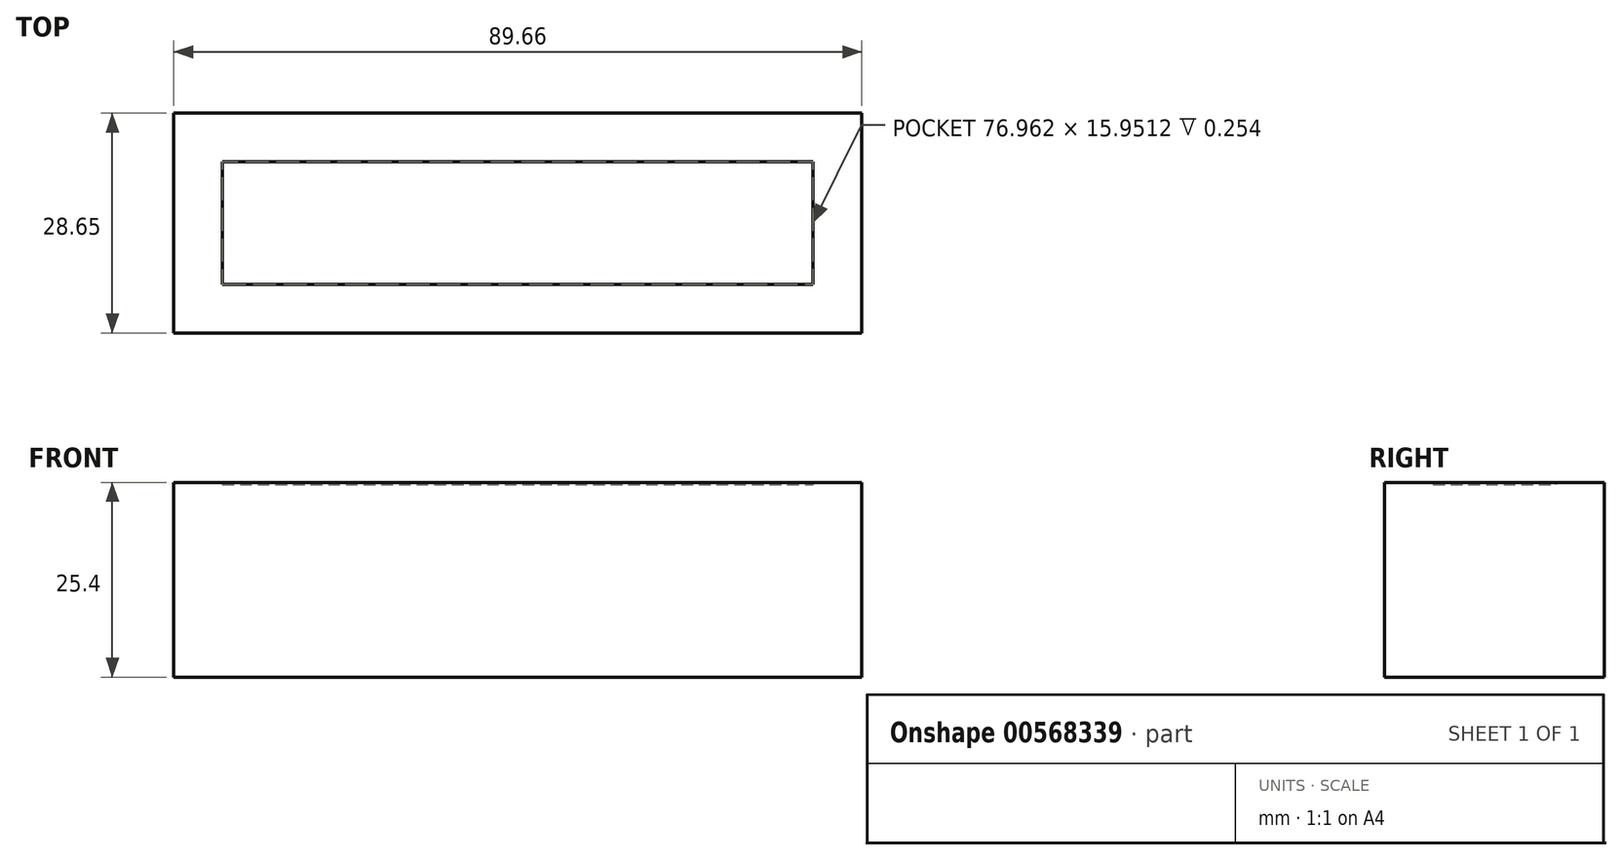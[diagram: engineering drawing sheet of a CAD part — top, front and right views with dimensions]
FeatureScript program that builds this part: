
annotation { "Feature Type Name" : "Feature", "Feature Type Description" : "" }
export const myFeature = defineFeature(function(context is Context, id is Id, definition is map)
    precondition{}
    {
        {
            var Q0;
            Q0=qCreatedBy(makeId("Top.planeOp"),FACE);
            var sketch = newSketch(context, id + "F0", { "sketchPlane" : qUnion([Q0])});
            skLineSegment(sketch, "E0.bottom", {"start": v(0, 0) * mm, "end": v(76.96, 0) * mm});
            skLineSegment(sketch, "E0.top", {"start": v(0, 15.95) * mm, "end": v(76.96, 15.95) * mm});
            skLineSegment(sketch, "E0.left", {"start": v(0, 0) * mm, "end": v(0, 15.95) * mm});
            skLineSegment(sketch, "E0.right", {"start": v(76.96, 0) * mm, "end": v(76.96, 15.95) * mm});
            skSolve(sketch);
        }
        {
            var Q0;
            Q0=makeQuery(id+"F0.imprint","IMPRINT",FACE,{"disambiguationData":[TD([[makeQuery(id+"F0.imprint","IMPRINT",EDGE,{"derivedFrom":sQuery(id+"F0.wireOp",EDGE,"E0.bottom")}),1.0]])]});
            extrude(context, id + "F1", {"entities" : qUnion([Q0]), "depth" : 0.25 * mm, "offsetDistance" : 25.4 * mm});
        }
        {
            var Q0;
            Q0=makeQuery(id+"F1.opExtrude","CAP_FACE",FACE,{"disambiguationData":[OSD([sQuery(id+"F0.wireOp",EDGE,"E0.bottom"),sQuery(id+"F0.wireOp",EDGE,"E0.top"),sQuery(id+"F0.wireOp",EDGE,"E0.left"),sQuery(id+"F0.wireOp",EDGE,"E0.right")])],"isStart":false});
            cPlane(context, id + "F2", {"entities" : qUnion([Q0]), "cplaneType" : CPlaneType.OFFSET, "offset" : 0 * mm, "width" : 152.4 * mm, "height" : 152.4 * mm});
        }
        {
            var Q0;
            Q0=qCreatedBy(id+"F2.planeOp",FACE);
            var sketch = newSketch(context, id + "F3", { "sketchPlane" : qUnion([Q0])});
            skLineSegment(sketch, "E1.0", {"start": v(0, 15.95) * mm, "end": v(76.96, 15.95) * mm});
            skLineSegment(sketch, "E2.0", {"start": v(76.96, 0) * mm, "end": v(76.96, 15.95) * mm});
            skLineSegment(sketch, "E3.0", {"start": v(0, 0) * mm, "end": v(76.96, 0) * mm});
            skLineSegment(sketch, "E4.0", {"start": v(0, 0) * mm, "end": v(0, 15.95) * mm});
            skLineSegment(sketch, "E5.0", {"start": v(-6.35, 22.3) * mm, "end": v(83.31, 22.3) * mm});
            skLineSegment(sketch, "E5.1", {"start": v(-6.35, -6.35) * mm, "end": v(-6.35, 22.3) * mm});
            skLineSegment(sketch, "E5.2", {"start": v(-6.35, -6.35) * mm, "end": v(83.31, -6.35) * mm});
            skLineSegment(sketch, "E5.3", {"start": v(83.31, -6.35) * mm, "end": v(83.31, 22.3) * mm});
            skSolve(sketch);
        }
        {
            var Q0;
            Q0=makeQuery(id+"F3.imprint","IMPRINT",FACE,{"disambiguationData":[TD([[makeQuery(id+"F3.imprint","IMPRINT",EDGE,{"derivedFrom":sQuery(id+"F3.wireOp",EDGE,"E1.0")}),1.0]])]});
            var Q1;
            Q1=makeQuery(id+"F3.imprint","IMPRINT",FACE,{"disambiguationData":[TD([[makeQuery(id+"F3.imprint","IMPRINT",EDGE,{"derivedFrom":sQuery(id+"F3.wireOp",EDGE,"E1.0")}),-1.0]])]});
            extrude(context, id + "F4", {"entities" : qUnion([Q0, Q1]), "oppositeDirection" : true, "depth" : 25.4 * mm, "offsetDistance" : 25.4 * mm});
        }
        {
            var Q0;
            Q0=makeQuery(id+"F1.opExtrude","SWEPT_BODY",BODY,{"disambiguationData":[OSD([sQuery(id+"F0.wireOp",EDGE,"E0.bottom"),sQuery(id+"F0.wireOp",EDGE,"E0.top"),sQuery(id+"F0.wireOp",EDGE,"E0.left"),sQuery(id+"F0.wireOp",EDGE,"E0.right")])]});
            var Q1;
            Q1=makeQuery(id+"F4.opExtrude","SWEPT_BODY",BODY,{"disambiguationData":[OSD([sQuery(id+"F3.wireOp",EDGE,"E5.0"),sQuery(id+"F3.wireOp",EDGE,"E5.1"),sQuery(id+"F3.wireOp",EDGE,"E5.2"),sQuery(id+"F3.wireOp",EDGE,"E5.3")])]});
            booleanBodies(context, id + "F5", {"operationType" : BooleanOperationType.SUBTRACTION, "tools" : qUnion([Q0]), "targets" : qUnion([Q1]), "keepTools" : true});
        }
    });
